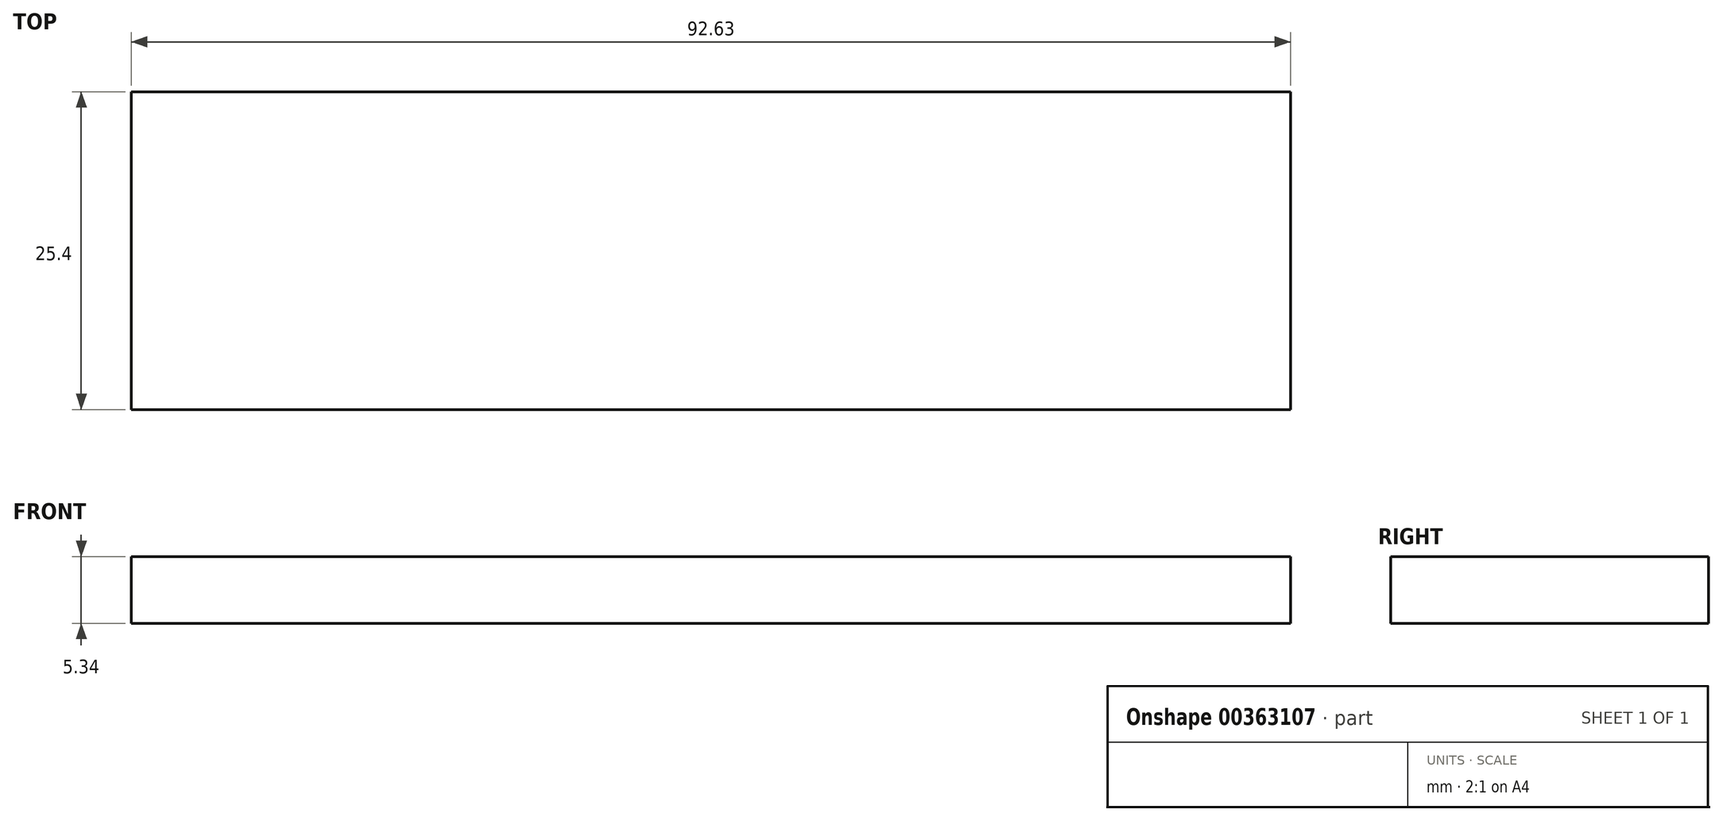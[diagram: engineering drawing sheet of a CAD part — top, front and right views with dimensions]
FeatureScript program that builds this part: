
annotation { "Feature Type Name" : "Feature", "Feature Type Description" : "" }
export const myFeature = defineFeature(function(context is Context, id is Id, definition is map)
    precondition{}
    {
        {
            var Q0;
            Q0=qCreatedBy(makeId("Front.planeOp"),FACE);
            var sketch = newSketch(context, id + "F0", { "sketchPlane" : qUnion([Q0])});
            skLineSegment(sketch, "E0.bottom", {"start": v(-44.91, 33.96) * mm, "end": v(47.72, 33.96) * mm});
            skLineSegment(sketch, "E0.top", {"start": v(-44.91, 28.62) * mm, "end": v(47.72, 28.62) * mm});
            skLineSegment(sketch, "E0.left", {"start": v(-44.91, 33.96) * mm, "end": v(-44.91, 28.62) * mm});
            skLineSegment(sketch, "E0.right", {"start": v(47.72, 33.96) * mm, "end": v(47.72, 28.62) * mm});
            skSolve(sketch);
        }
        {
            var Q0;
            Q0=sQuery(id+"F0.wireOp",EDGE,"E0.bottom");
            var Q1;
            Q1=sQuery(id+"F0.wireOp",EDGE,"E0.top");
            var Q2;
            Q2=sQuery(id+"F0.wireOp",EDGE,"E0.right");
            var Q3;
            Q3=sQuery(id+"F0.wireOp",EDGE,"E0.left");
            extrude(context, id + "F1", {"bodyType" : ToolBodyType.SURFACE, "surfaceEntities" : qUnion([Q0, Q1, Q2, Q3]), "depth" : 25.4 * mm});
        }
    });
